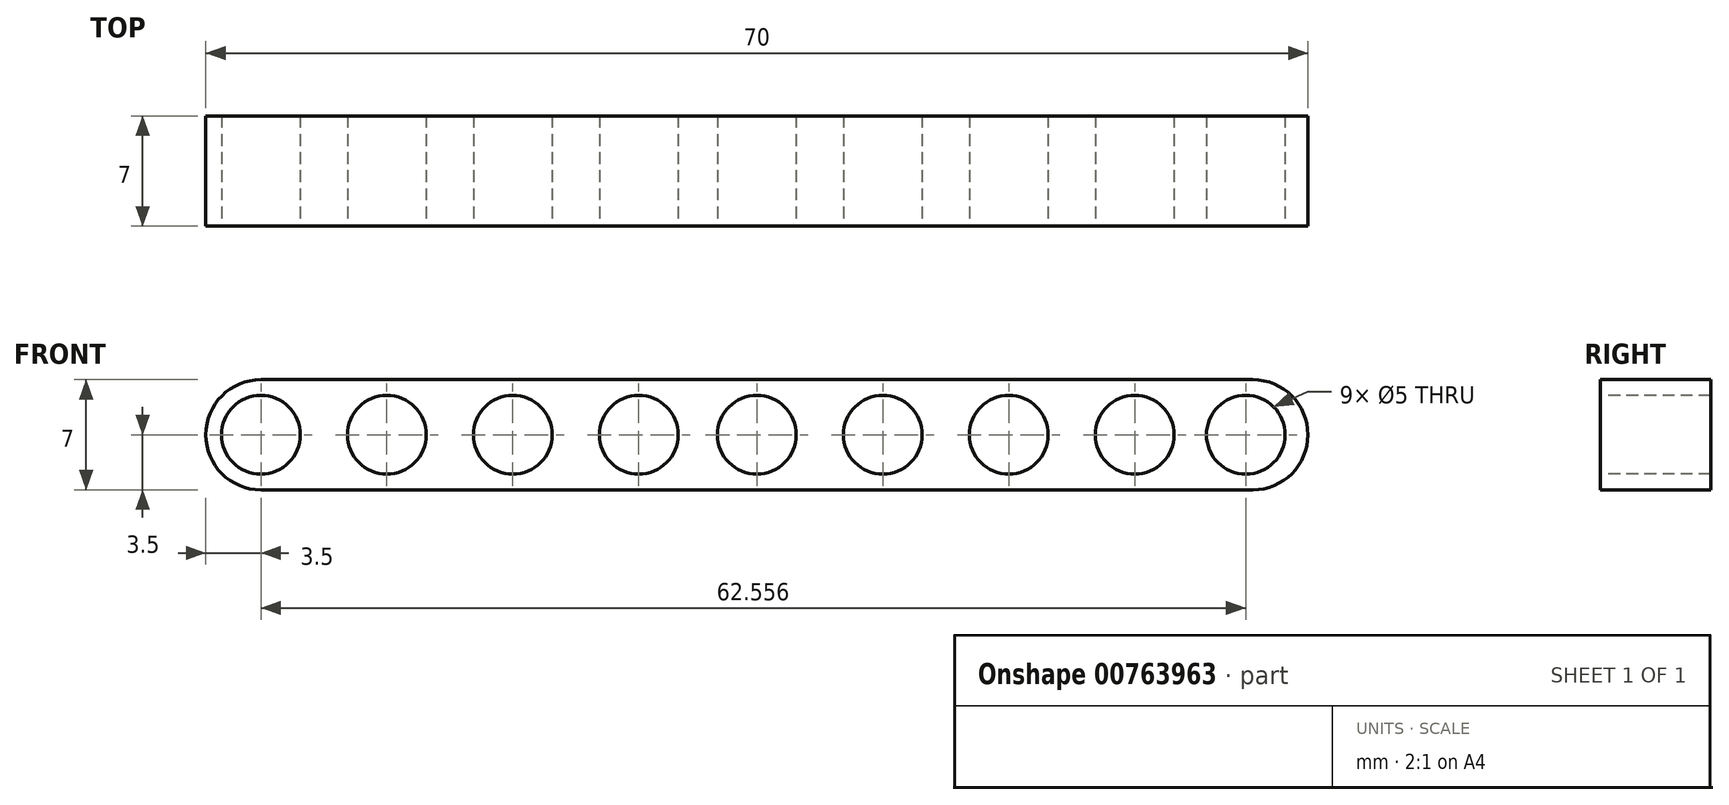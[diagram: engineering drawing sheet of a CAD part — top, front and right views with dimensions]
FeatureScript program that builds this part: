
annotation { "Feature Type Name" : "Feature", "Feature Type Description" : "" }
export const myFeature = defineFeature(function(context is Context, id is Id, definition is map)
    precondition{}
    {
        {
            var Q0;
            Q0=qCreatedBy(makeId("Front.planeOp"),FACE);
            var sketch = newSketch(context, id + "F0", { "sketchPlane" : qUnion([Q0])});
            skLineSegment(sketch, "E0.bottom", {"start": v(31.5, -3.5) * mm, "end": v(-31.5, -3.5) * mm});
            skLineSegment(sketch, "E0.top", {"start": v(31.5, 3.5) * mm, "end": v(-31.5, 3.5) * mm});
            skLineSegment(sketch, "E0.left", {"start": v(35, 0) * mm, "end": v(35, 0) * mm});
            skLineSegment(sketch, "E0.right", {"start": v(-35, 0) * mm, "end": v(-35, 0) * mm});
            skPoint(sketch, "E0.middle", {"position": v(0, 0) * mm});
            skPoint(sketch, "E1.visualSharp", {"position": v(-35, 3.5) * mm});
            skArc(sketch, "E1.filletArc", {"start": v(-31.5, 3.5) * mm, "mid": v(-33.97, 2.47) * mm, "end": v(-35, 0) * mm});
            skPoint(sketch, "E2.visualSharp", {"position": v(-35, -3.5) * mm});
            skArc(sketch, "E2.filletArc", {"start": v(-35, 0) * mm, "mid": v(-33.97, -2.47) * mm, "end": v(-31.5, -3.5) * mm});
            skPoint(sketch, "E3.visualSharp", {"position": v(35, 3.5) * mm});
            skArc(sketch, "E3.filletArc", {"start": v(35, 0) * mm, "mid": v(33.97, 2.47) * mm, "end": v(31.5, 3.5) * mm});
            skPoint(sketch, "E4.visualSharp", {"position": v(35, -3.5) * mm});
            skArc(sketch, "E4.filletArc", {"start": v(31.5, -3.5) * mm, "mid": v(33.97, -2.47) * mm, "end": v(35, 0) * mm});
            skSolve(sketch);
        }
        {
            var Q0;
            Q0=makeQuery(id+"F0.imprint","IMPRINT",FACE,{"disambiguationData":[TD([[makeQuery(id+"F0.imprint","IMPRINT",EDGE,{"derivedFrom":sQuery(id+"F0.wireOp",EDGE,"E0.bottom")}),-1.0]])]});
            extrude(context, id + "F1", {"entities" : qUnion([Q0]), "depth" : 7 * mm, "offsetDistance" : 25 * mm});
        }
        {
            var Q0;
            Q0=makeQuery(id+"F1.opExtrude","CAP_FACE",FACE,{"disambiguationData":[OSD([sQuery(id+"F0.wireOp",EDGE,"E0.bottom"),sQuery(id+"F0.wireOp",EDGE,"E0.top"),sQuery(id+"F0.wireOp",EDGE,"E1.filletArc"),sQuery(id+"F0.wireOp",EDGE,"E2.filletArc"),sQuery(id+"F0.wireOp",EDGE,"E3.filletArc"),sQuery(id+"F0.wireOp",EDGE,"E4.filletArc")])],"isStart":false});
            var sketch = newSketch(context, id + "F2", { "sketchPlane" : qUnion([Q0])});
            skSolve(sketch);
        }
        {
            var Q0;
            Q0=makeQuery(id+"F2.imprint","IMPRINT",FACE,{"disambiguationData":[TD([[makeQuery(id+"F2.imprint","IMPRINT",EDGE,{"derivedFrom":makeQuery(id+"F1.opExtrude","CAP_EDGE",EDGE,{"disambiguationData":[OSD([sQuery(id+"F0.wireOp",EDGE,"E0.bottom")])],"isStart":false})}),-1.0]])]});
            var sketch = newSketch(context, id + "F3", { "sketchPlane" : qUnion([Q0])});
            skLineSegment(sketch, "E5", {"start": v(34.56, 0) * mm, "end": v(-35.75, 0) * mm});
            skCircle(sketch, "E6", {"center": v(-31.5, 0) * mm, "radius": 2.5 * mm});
            skCircle(sketch, "E7", {"center": v(-23.5, 0) * mm, "radius": 2.5 * mm});
            skCircle(sketch, "E8", {"center": v(-15.5, 0) * mm, "radius": 2.5 * mm});
            skCircle(sketch, "E9", {"center": v(-7.5, 0) * mm, "radius": 2.5 * mm});
            skCircle(sketch, "E10", {"center": v(0, 0) * mm, "radius": 2.5 * mm});
            skCircle(sketch, "E11", {"center": v(8, 0) * mm, "radius": 2.5 * mm});
            skCircle(sketch, "E12", {"center": v(16, 0) * mm, "radius": 2.5 * mm});
            skCircle(sketch, "E13", {"center": v(24, 0) * mm, "radius": 2.5 * mm});
            skCircle(sketch, "E14", {"center": v(31.06, 0) * mm, "radius": 2.5 * mm});
            skSolve(sketch);
        }
        {
            var Q0;
            Q0 = qSketchRegion(id + "F3", true);
            extrude(context, id + "F4", {"entities" : qUnion([Q0]), "operationType" : NewBodyOperationType.REMOVE, "endBound" : BoundingType.THROUGH_ALL, "oppositeDirection" : true, "depth" : 25 * mm, "offsetDistance" : 25 * mm});
        }
    });
